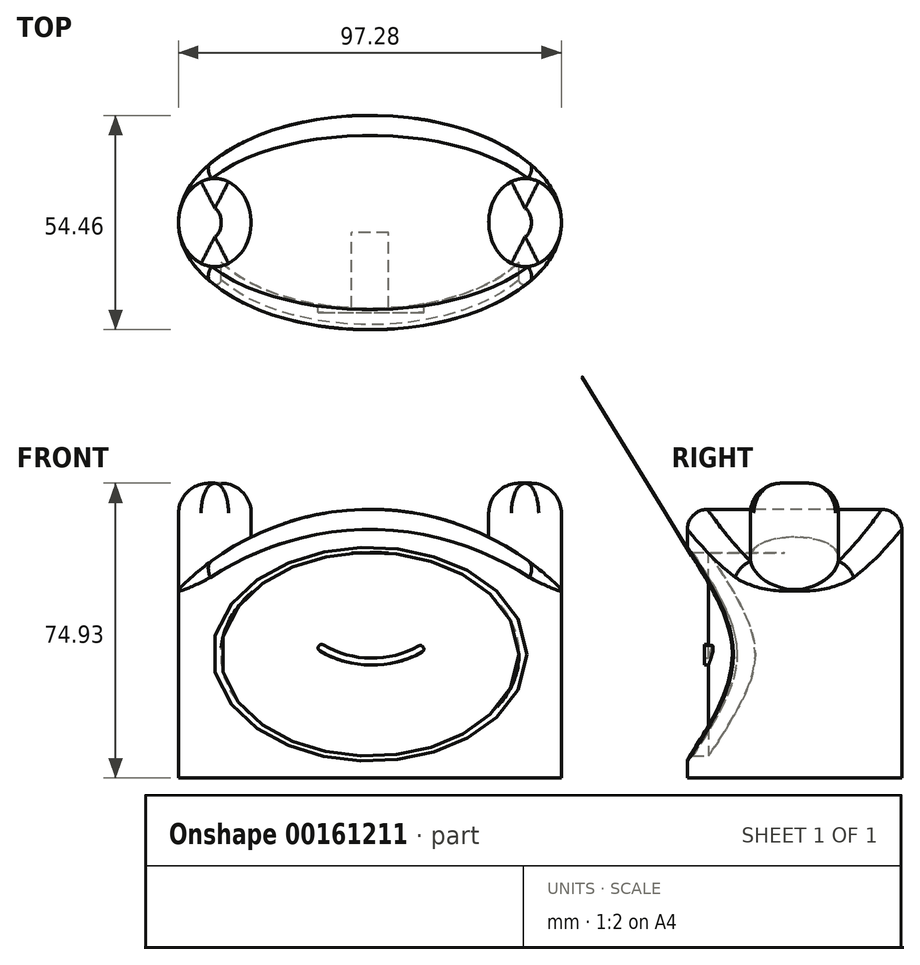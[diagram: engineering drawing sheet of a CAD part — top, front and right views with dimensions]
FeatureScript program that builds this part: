
annotation { "Feature Type Name" : "Feature", "Feature Type Description" : "" }
export const myFeature = defineFeature(function(context is Context, id is Id, definition is map)
    precondition{}
    {
        {
            var Q0;
            Q0=qCreatedBy(makeId("Top.planeOp"),FACE);
            var sketch = newSketch(context, id + "F0", { "sketchPlane" : qUnion([Q0])});
            skEllipse(sketch, "E0", {"center": v(0, 0) * mm, "majorRadius": 48.64 * mm, "minorRadius": 27.23 * mm, "majorAxis": v(1, 0)});
            skSolve(sketch);
        }
        {
            var Q0;
            Q0=makeQuery(id+"F0.imprint","IMPRINT",FACE,{"disambiguationData":[TD([[makeQuery(id+"F0.imprint","IMPRINT",EDGE,{"derivedFrom":sQuery(id+"F0.wireOp",EDGE,"E0")}),1.0]])]});
            extrude(context, id + "F1", {"entities" : qUnion([Q0]), "depth" : 73.02 * mm});
        }
        {
            var Q0;
            Q0=qCreatedBy(makeId("Front.planeOp"),FACE);
            var sketch = newSketch(context, id + "F2", { "sketchPlane" : qUnion([Q0])});
            skArc(sketch, "E1", {"start": v(56.39, 38.52) * mm, "mid": v(1.63, 68.27) * mm, "end": v(-54.48, 41.17) * mm});
            skLineSegment(sketch, "E2", {"start": v(-54.48, 41.17) * mm, "end": v(-54.48, 78.36) * mm});
            skLineSegment(sketch, "E3", {"start": v(-54.48, 78.36) * mm, "end": v(59.45, 78.36) * mm});
            skLineSegment(sketch, "E4", {"start": v(59.45, 78.36) * mm, "end": v(56.39, 38.52) * mm});
            skSolve(sketch);
        }
        {
            var Q0;
            Q0 = qSketchRegion(id + "F2", true);
            extrude(context, id + "F3", {"entities" : qUnion([Q0]), "operationType" : NewBodyOperationType.REMOVE, "endBound" : BoundingType.SYMMETRIC, "oppositeDirection" : true, "depth" : 101.6 * mm});
        }
        {
            var Q0;
            Q0=qCreatedBy(makeId("Top.planeOp"),FACE);
            var sketch = newSketch(context, id + "F4", { "sketchPlane" : qUnion([Q0])});
            skEllipse(sketch, "E5", {"center": v(-39.4, 0) * mm, "majorRadius": 9.23 * mm, "minorRadius": 11.2 * mm, "majorAxis": v(1, 0)});
            skEllipse(sketch, "E6.MirrorC", {"center": v(39.4, 0) * mm, "majorRadius": 9.23 * mm, "minorRadius": 11.2 * mm, "majorAxis": v(-1, 0)});
            skSolve(sketch);
        }
        {
            var Q0;
            Q0 = qSketchRegion(id + "F4", true);
            extrude(context, id + "F5", {"entities" : qUnion([Q0]), "operationType" : NewBodyOperationType.ADD, "depth" : 74.93 * mm});
        }
        {
            var Q0;
            Q0=qCreatedBy(makeId("Front.planeOp"),FACE);
            var sketch = newSketch(context, id + "F6", { "sketchPlane" : qUnion([Q0])});
            skEllipse(sketch, "E7", {"center": v(0, 31.47) * mm, "majorRadius": 37.87 * mm, "minorRadius": 25.88 * mm, "majorAxis": v(1, 0)});
            skSolve(sketch);
        }
        {
            var Q0;
            Q0 = qSketchRegion(id + "F6", true);
            extrude(context, id + "F7", {"entities" : qUnion([Q0]), "operationType" : NewBodyOperationType.REMOVE, "depth" : 38.1 * mm, "hasSecondDirection" : true, "secondDirectionOppositeDirection" : false, "secondDirectionDepth" : 2.54 * mm});
        }
        {
            var Q0;
            Q0=qCreatedBy(makeId("Top.planeOp"),FACE);
            var sketch = newSketch(context, id + "F8", { "sketchPlane" : qUnion([Q0])});
            skEllipse(sketch, "E8", {"center": v(0, 0) * mm, "majorRadius": 42.58 * mm, "minorRadius": 21.86 * mm, "majorAxis": v(1, 0)});
            skSolve(sketch);
        }
        {
            var Q0;
            Q0 = qSketchRegion(id + "F8", true);
            extrude(context, id + "F9", {"entities" : qUnion([Q0]), "operationType" : NewBodyOperationType.ADD, "depth" : 57.15 * mm});
        }
        {
            var Q0;
            Q0=qCreatedBy(makeId("Front.planeOp"),FACE);
            var sketch = newSketch(context, id + "F10", { "sketchPlane" : qUnion([Q0])});
            skCircle(sketch, "E9", {"center": v(-19.96, 36.8) * mm, "radius": 3.04 * mm});
            skCircle(sketch, "E10.MirrorC", {"center": v(19.96, 36.8) * mm, "radius": 3.04 * mm});
            skSolve(sketch);
        }
        {
            var Q0;
            Q0=sQuery(id+"F10.wireOp",EDGE,"E9");
            var Q1;
            Q1=sQuery(id+"F10.wireOp",EDGE,"E10.MirrorC");
            extrude(context, id + "F11", {"bodyType" : ToolBodyType.SURFACE, "surfaceEntities" : qUnion([Q0, Q1]), "depth" : 22.86 * mm});
        }
        {
            var Q0;
            Q0=qCreatedBy(makeId("Front.planeOp"),FACE);
            var sketch = newSketch(context, id + "F12", { "sketchPlane" : qUnion([Q0])});
            skArc(sketch, "E11", {"start": v(-12.27, 33.07) * mm, "mid": v(0.23, 29.6) * mm, "end": v(12.8, 32.8) * mm});
            skArc(sketch, "E12.0.startCap", {"start": v(-12.72, 32.3) * mm, "mid": v(-13.03, 33.52) * mm, "end": v(-11.82, 33.84) * mm});
            skArc(sketch, "E12.0.endCap", {"start": v(12.37, 33.58) * mm, "mid": v(13.58, 33.24) * mm, "end": v(13.24, 32.03) * mm});
            skArc(sketch, "E12.0.left", {"start": v(-11.82, 33.84) * mm, "mid": v(0.24, 30.48) * mm, "end": v(12.37, 33.58) * mm});
            skArc(sketch, "E12.0.right", {"start": v(-12.72, 32.3) * mm, "mid": v(0.22, 28.7) * mm, "end": v(13.24, 32.03) * mm});
            skSolve(sketch);
        }
        {
            var Q0;
            Q0=makeQuery(id+"F5.opExtrude","CAP_EDGE",EDGE,{"disambiguationData":[OSD([sQuery(id+"F4.wireOp",EDGE,"E6.MirrorC")])],"isStart":false});
            var Q1;
            Q1=makeQuery(id+"F5.opExtrude","CAP_EDGE",EDGE,{"disambiguationData":[OSD([sQuery(id+"F4.wireOp",EDGE,"E5")])],"isStart":false});
            fillet(context, id + "F13", {"entities" : qUnion([Q0, Q1]), "radius" : 7.62 * mm, "tangentPropagation" : true, "allowEdgeOverflow" : false});
        }
        {
            var Q0;
            Q0=makeQuery(id+"F3.boolean.opBoolean","INTERSECT",EDGE,{"derivedFrom":[makeQuery(id+"F1.opExtrude","SWEPT_FACE",FACE,{"disambiguationData":[OSD([sQuery(id+"F0.wireOp",EDGE,"E0")])]}),makeQuery(id+"F3.opExtrude","SWEPT_FACE",FACE,{"disambiguationData":[OSD([sQuery(id+"F2.wireOp",EDGE,"E1")])]})]});
            fillet(context, id + "F14", {"entities" : qUnion([Q0]), "radius" : 5.08 * mm, "tangentPropagation" : true, "allowEdgeOverflow" : false});
        }
        {
            var Q0;
            Q0=makeQuery(id+"F7.boolean.opBoolean","INTERSECT",EDGE,{"derivedFrom":[makeQuery(id+"F1.opExtrude","SWEPT_FACE",FACE,{"disambiguationData":[OSD([sQuery(id+"F0.wireOp",EDGE,"E0")])]}),makeQuery(id+"F7.opExtrude","SWEPT_FACE",FACE,{"disambiguationData":[OSD([sQuery(id+"F6.wireOp",EDGE,"E7")])]})]});
            fillet(context, id + "F15", {"entities" : qUnion([Q0]), "radius" : 1.27 * mm, "tangentPropagation" : true, "allowEdgeOverflow" : false});
        }
        {
            var Q0;
            Q0 = qSketchRegion(id + "F12", true);
            extrude(context, id + "F16", {"entities" : qUnion([Q0]), "operationType" : NewBodyOperationType.ADD, "depth" : 22.86 * mm});
        }
    });
